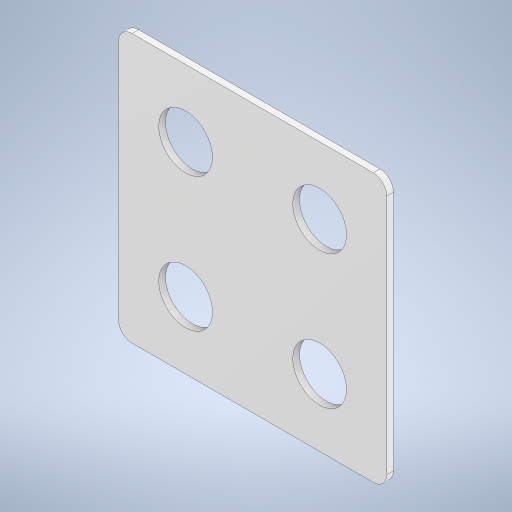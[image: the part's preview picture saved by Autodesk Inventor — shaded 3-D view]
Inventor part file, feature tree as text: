
AUTODESK INVENTOR PART (.ipt)
format: ipt  version: 2024 (Build 280153000, 153)  size: 249,344 bytes
history: native  units: mm
features: fillet x3, extrude x2, sketch x2, other x1, pattern_linear x1
ambient origin geometry x8: Origin, YZ Plane, XZ Plane, XY Plane, X Axis, Y Axis, Z Axis, Center Point
bodies: Body1 (feature_tree)
feature tree (9):
  other  "Těleso1"
  extrude  "Vysunutí1"  Depth=20.0mm
  extrude  "Vysunutí2"  Depth=20.0mm
  pattern_linear  "Obdélníkové pole1"  Spacing1=10.0mm  [1 undecoded]
  fillet  "Zaoblení1"  Radius=10.0mm
  fillet  "Zaoblení2"  Radius=0.5mm
  fillet  "Zaoblení3"  Radius=4.0mm
  sketch  "Náčrt1"
  sketch  "Náčrt2"
note: 1 required parameter value undecoded (feature->parameter linkage not recoverable at this tier; creation-order binding heuristic only, values carry confidence <= 0.55)
